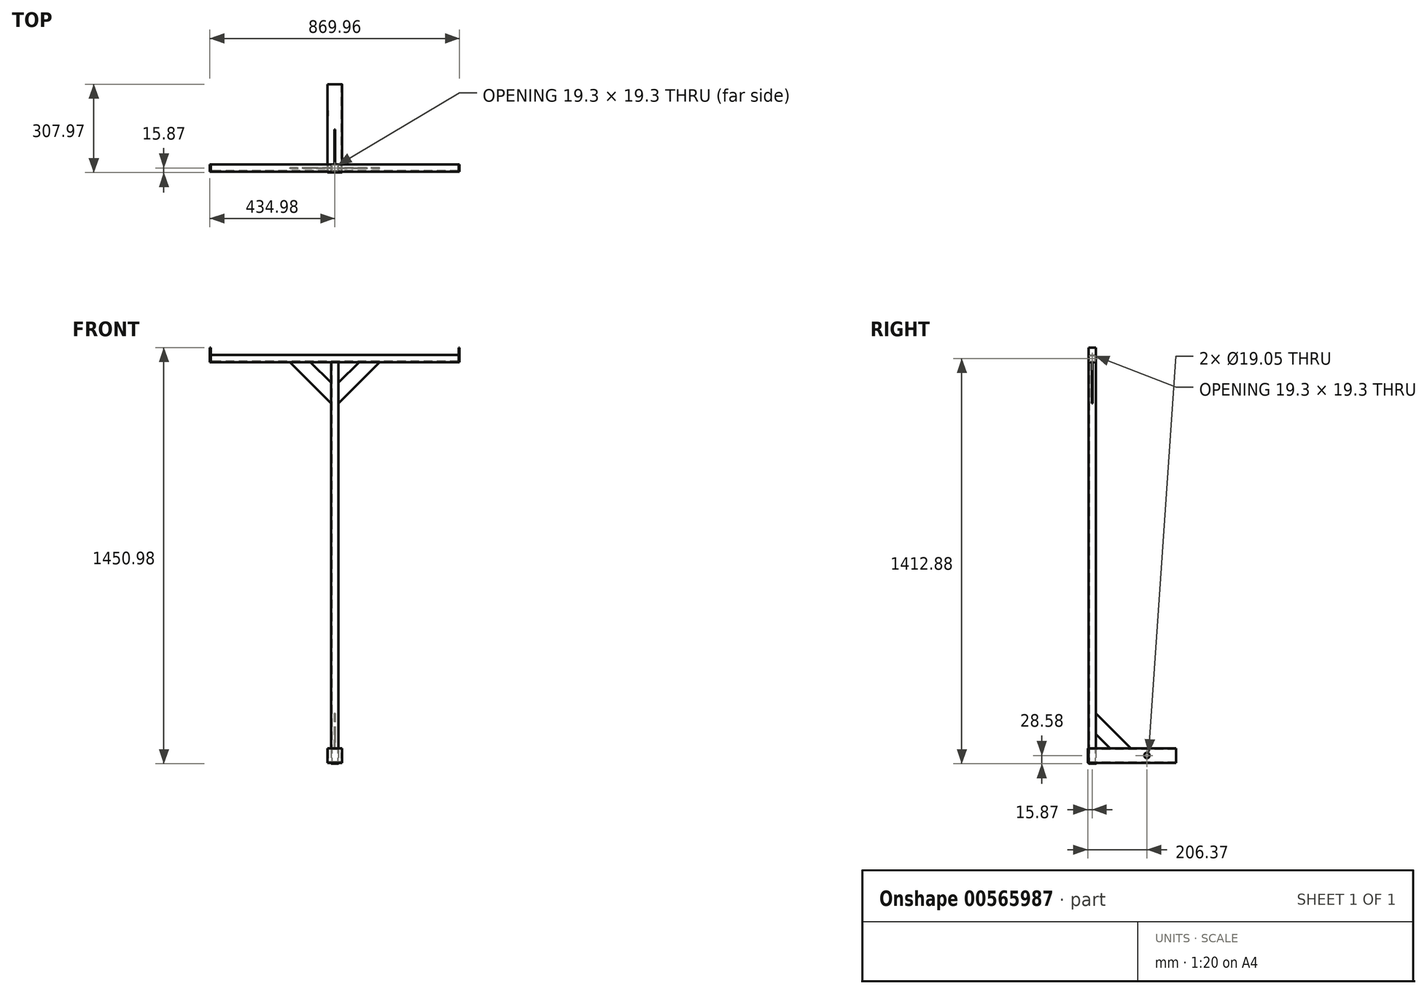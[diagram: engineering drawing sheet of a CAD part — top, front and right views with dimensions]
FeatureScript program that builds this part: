
annotation { "Feature Type Name" : "Feature", "Feature Type Description" : "" }
export const myFeature = defineFeature(function(context is Context, id is Id, definition is map)
    precondition{}
    {
        {
            var Q0;
            Q0=qCreatedBy(makeId("Front.planeOp"),FACE);
            var sketch = newSketch(context, id + "F0", { "sketchPlane" : qUnion([Q0])});
            skLineSegment(sketch, "E0.bottom", {"start": v(20.32, 25.4) * mm, "end": v(-20.32, 25.4) * mm});
            skLineSegment(sketch, "E0.top", {"start": v(20.32, -25.4) * mm, "end": v(-20.32, -25.4) * mm});
            skLineSegment(sketch, "E0.left", {"start": v(25.4, 20.32) * mm, "end": v(25.4, -20.32) * mm});
            skLineSegment(sketch, "E0.right", {"start": v(-25.4, 20.32) * mm, "end": v(-25.4, -20.32) * mm});
            skPoint(sketch, "E1.visualSharp", {"position": v(-25.4, 25.4) * mm});
            skArc(sketch, "E1.filletArc", {"start": v(-20.32, 25.4) * mm, "mid": v(-23.91, 23.91) * mm, "end": v(-25.4, 20.32) * mm});
            skPoint(sketch, "E2.visualSharp", {"position": v(25.4, 25.4) * mm});
            skArc(sketch, "E2.filletArc", {"start": v(25.4, 20.32) * mm, "mid": v(23.91, 23.91) * mm, "end": v(20.32, 25.4) * mm});
            skPoint(sketch, "E3.visualSharp", {"position": v(25.4, -25.4) * mm});
            skArc(sketch, "E3.filletArc", {"start": v(20.32, -25.4) * mm, "mid": v(23.91, -23.91) * mm, "end": v(25.4, -20.32) * mm});
            skPoint(sketch, "E4.visualSharp", {"position": v(-25.4, -25.4) * mm});
            skArc(sketch, "E4.filletArc", {"start": v(-25.4, -20.32) * mm, "mid": v(-23.91, -23.91) * mm, "end": v(-20.32, -25.4) * mm});
            skLineSegment(sketch, "E5.0", {"start": v(20.32, -22.35) * mm, "end": v(-20.32, -22.35) * mm});
            skArc(sketch, "E5.1", {"start": v(-22.35, -20.32) * mm, "mid": v(-21.76, -21.76) * mm, "end": v(-20.32, -22.35) * mm});
            skArc(sketch, "E5.2", {"start": v(20.32, -22.35) * mm, "mid": v(21.76, -21.76) * mm, "end": v(22.35, -20.32) * mm});
            skLineSegment(sketch, "E5.3", {"start": v(-22.35, 20.32) * mm, "end": v(-22.35, -20.32) * mm});
            skLineSegment(sketch, "E5.4", {"start": v(22.35, 20.32) * mm, "end": v(22.35, -20.32) * mm});
            skArc(sketch, "E5.5", {"start": v(22.35, 20.32) * mm, "mid": v(21.76, 21.76) * mm, "end": v(20.32, 22.35) * mm});
            skLineSegment(sketch, "E5.6", {"start": v(20.32, 22.35) * mm, "end": v(-20.32, 22.35) * mm});
            skArc(sketch, "E5.7", {"start": v(-20.32, 22.35) * mm, "mid": v(-21.76, 21.76) * mm, "end": v(-22.35, 20.32) * mm});
            skSolve(sketch);
        }
        {
            var Q0;
            Q0 = qSketchRegion(id + "F0", true);
            extrude(context, id + "F1", {"entities" : qUnion([Q0]), "endBound" : BoundingType.SYMMETRIC, "depth" : 304.8 * mm, "offsetDistance" : 25.4 * mm});
        }
        {
            var Q0;
            Q0=qCreatedBy(makeId("Top.planeOp"),FACE);
            var sketch = newSketch(context, id + "F2", { "sketchPlane" : qUnion([Q0])});
            skLineSegment(sketch, "E6.bottom", {"start": v(12.7, -127) * mm, "end": v(-12.7, -127) * mm});
            skLineSegment(sketch, "E6.top", {"start": v(12.7, -152.4) * mm, "end": v(-12.7, -152.4) * mm});
            skLineSegment(sketch, "E6.left", {"start": v(12.7, -127) * mm, "end": v(12.7, -152.4) * mm});
            skLineSegment(sketch, "E6.right", {"start": v(-12.7, -127) * mm, "end": v(-12.7, -152.4) * mm});
            skPoint(sketch, "E6.middle", {"position": v(0, -139.7) * mm});
            skSolve(sketch);
        }
        {
            var Q0;
            Q0 = qSketchRegion(id + "F2", true);
            extrude(context, id + "F3", {"entities" : qUnion([Q0]), "operationType" : NewBodyOperationType.REMOVE, "endBound" : BoundingType.SYMMETRIC, "oppositeDirection" : true, "depth" : 50.8 * mm, "offsetDistance" : 25.4 * mm});
        }
        {
            var Q0;
            Q0=qCreatedBy(makeId("Right.planeOp"),FACE);
            var sketch = newSketch(context, id + "F4", { "sketchPlane" : qUnion([Q0])});
            skCircle(sketch, "E7", {"center": v(50.8, 0) * mm, "radius": 9.53 * mm});
            skSolve(sketch);
        }
        {
            var Q0;
            Q0=qCreatedBy(makeId("Top.planeOp"),FACE);
            var sketch = newSketch(context, id + "F5", { "sketchPlane" : qUnion([Q0])});
            skLineSegment(sketch, "E8.bottom", {"start": v(9.53, -127) * mm, "end": v(-9.52, -127) * mm});
            skLineSegment(sketch, "E8.top", {"start": v(9.53, -152.4) * mm, "end": v(-9.52, -152.4) * mm});
            skLineSegment(sketch, "E8.left", {"start": v(12.7, -130.18) * mm, "end": v(12.7, -149.22) * mm});
            skLineSegment(sketch, "E8.right", {"start": v(-12.7, -130.18) * mm, "end": v(-12.7, -149.22) * mm});
            skPoint(sketch, "E8.middle", {"position": v(0, -139.7) * mm});
            skPoint(sketch, "E9.visualSharp", {"position": v(-12.7, -127) * mm});
            skArc(sketch, "E9.filletArc", {"start": v(-9.52, -127) * mm, "mid": v(-11.77, -127.93) * mm, "end": v(-12.7, -130.18) * mm});
            skPoint(sketch, "E10.visualSharp", {"position": v(12.7, -127) * mm});
            skArc(sketch, "E10.filletArc", {"start": v(12.7, -130.18) * mm, "mid": v(11.77, -127.93) * mm, "end": v(9.53, -127) * mm});
            skPoint(sketch, "E11.visualSharp", {"position": v(12.7, -152.4) * mm});
            skArc(sketch, "E11.filletArc", {"start": v(9.53, -152.4) * mm, "mid": v(11.77, -151.47) * mm, "end": v(12.7, -149.22) * mm});
            skPoint(sketch, "E12.visualSharp", {"position": v(-12.7, -152.4) * mm});
            skArc(sketch, "E12.filletArc", {"start": v(-12.7, -149.22) * mm, "mid": v(-11.77, -151.47) * mm, "end": v(-9.52, -152.4) * mm});
            skArc(sketch, "E13.0", {"start": v(9.53, -149.35) * mm, "mid": v(9.61, -149.31) * mm, "end": v(9.65, -149.22) * mm});
            skLineSegment(sketch, "E13.1", {"start": v(9.65, -130.18) * mm, "end": v(9.65, -149.22) * mm});
            skLineSegment(sketch, "E13.2", {"start": v(9.53, -149.35) * mm, "end": v(-9.52, -149.35) * mm});
            skArc(sketch, "E13.3", {"start": v(9.65, -130.18) * mm, "mid": v(9.61, -130.09) * mm, "end": v(9.53, -130.05) * mm});
            skArc(sketch, "E13.4", {"start": v(-9.65, -149.22) * mm, "mid": v(-9.61, -149.31) * mm, "end": v(-9.52, -149.35) * mm});
            skLineSegment(sketch, "E13.5", {"start": v(-9.65, -130.18) * mm, "end": v(-9.65, -149.22) * mm});
            skArc(sketch, "E13.6", {"start": v(-9.52, -130.05) * mm, "mid": v(-9.61, -130.09) * mm, "end": v(-9.65, -130.18) * mm});
            skLineSegment(sketch, "E13.7", {"start": v(9.53, -130.05) * mm, "end": v(-9.52, -130.05) * mm});
            skSolve(sketch);
        }
        {
            var Q0;
            Q0 = qSketchRegion(id + "F5", true);
            extrude(context, id + "F6", {"entities" : qUnion([Q0]), "depth" : 1371.6 * mm, "offsetDistance" : 25.4 * mm});
        }
        {
            var Q0;
            Q0 = qSketchRegion(id + "F5", true);
            extrude(context, id + "F7", {"entities" : qUnion([Q0]), "operationType" : NewBodyOperationType.ADD, "oppositeDirection" : true, "depth" : 28.57 * mm, "offsetDistance" : 25.4 * mm});
        }
        {
            var Q0;
            Q0 = qSketchRegion(id + "F4", true);
            extrude(context, id + "F8", {"entities" : qUnion([Q0]), "operationType" : NewBodyOperationType.REMOVE, "endBound" : BoundingType.SYMMETRIC, "oppositeDirection" : true, "depth" : 50.8 * mm, "offsetDistance" : 25.4 * mm});
        }
        {
            var Q0;
            {var subQ0=sQuery(id+"F0.wireOp",EDGE,"E5.3");var subQ1=sQuery(id+"F0.wireOp",EDGE,"E5.0");var subQ2=sQuery(id+"F0.wireOp",EDGE,"E4.filletArc");var subQ3=sQuery(id+"F0.wireOp",EDGE,"E5.1");var subQ4=sQuery(id+"F0.wireOp",EDGE,"E0.bottom");var subQ5=sQuery(id+"F0.wireOp",EDGE,"E5.6");var subQ6=sQuery(id+"F0.wireOp",EDGE,"E0.right");var subQ7=sQuery(id+"F0.wireOp",EDGE,"E0.top");var subQ8=sQuery(id+"F0.wireOp",EDGE,"E5.7");var subQ9=sQuery(id+"F0.wireOp",EDGE,"E1.filletArc");Q0=makeQuery(id+"F3.boolean.opBoolean","SPLIT",FACE,{"disambiguationData":[TD([makeQuery(id+"F1.opExtrude","SWEPT_FACE",FACE,{"disambiguationData":[OSD([subQ6])]})])],"derivedFrom":makeQuery(id+"F1.opExtrude","CAP_FACE",FACE,{"disambiguationData":[OSD([subQ4,subQ7,sQuery(id+"F0.wireOp",EDGE,"E0.left"),subQ6,subQ9,sQuery(id+"F0.wireOp",EDGE,"E2.filletArc"),sQuery(id+"F0.wireOp",EDGE,"E3.filletArc"),subQ2,subQ1,subQ3,sQuery(id+"F0.wireOp",EDGE,"E5.2"),subQ0,sQuery(id+"F0.wireOp",EDGE,"E5.4"),sQuery(id+"F0.wireOp",EDGE,"E5.5"),subQ5,subQ8])],"isStart":false})});}
            var sketch = newSketch(context, id + "F9", { "sketchPlane" : qUnion([Q0])});
            skLineSegment(sketch, "E14.bottom", {"start": v(-25.4, 25.4) * mm, "end": v(25.4, 25.4) * mm});
            skLineSegment(sketch, "E14.top", {"start": v(-25.4, -25.4) * mm, "end": v(25.4, -25.4) * mm});
            skLineSegment(sketch, "E14.left", {"start": v(-25.4, 25.4) * mm, "end": v(-25.4, -25.4) * mm});
            skLineSegment(sketch, "E14.right", {"start": v(25.4, 25.4) * mm, "end": v(25.4, -25.4) * mm});
            skPoint(sketch, "E14.middle", {"position": v(0, 0) * mm});
            skSolve(sketch);
        }
        {
            var Q0;
            Q0 = qSketchRegion(id + "F9", true);
            extrude(context, id + "F10", {"entities" : qUnion([Q0]), "depth" : 3.17 * mm, "offsetDistance" : 25.4 * mm});
        }
        {
            var Q0;
            Q0=qCreatedBy(makeId("Right.planeOp"),FACE);
            var sketch = newSketch(context, id + "F11", { "sketchPlane" : qUnion([Q0])});
            skLineSegment(sketch, "E15", {"start": v(-5.77, 25.4) * mm, "end": v(-127, 146.63) * mm});
            skLineSegment(sketch, "E16", {"start": v(-127, 146.63) * mm, "end": v(-127, 74.8) * mm});
            skLineSegment(sketch, "E17", {"start": v(-127, 74.8) * mm, "end": v(-77.6, 25.4) * mm});
            skLineSegment(sketch, "E18", {"start": v(-77.6, 25.4) * mm, "end": v(-5.77, 25.4) * mm});
            skSolve(sketch);
        }
        {
            var Q0;
            Q0 = qSketchRegion(id + "F11", true);
            extrude(context, id + "F12", {"entities" : qUnion([Q0]), "endBound" : BoundingType.SYMMETRIC, "depth" : 3.17 * mm, "offsetDistance" : 25.4 * mm});
        }
        {
            var Q0;
            Q0=qCreatedBy(makeId("Right.planeOp"),FACE);
            var sketch = newSketch(context, id + "F13", { "sketchPlane" : qUnion([Q0])});
            skLineSegment(sketch, "E19.bottom", {"start": v(-149.22, 1371.6) * mm, "end": v(-130.17, 1371.6) * mm});
            skLineSegment(sketch, "E19.top", {"start": v(-149.23, 1397) * mm, "end": v(-130.18, 1397) * mm});
            skLineSegment(sketch, "E19.left", {"start": v(-152.4, 1374.78) * mm, "end": v(-152.4, 1393.83) * mm});
            skLineSegment(sketch, "E19.right", {"start": v(-127, 1374.78) * mm, "end": v(-127, 1393.83) * mm});
            skPoint(sketch, "E19.middle", {"position": v(-139.7, 1384.3) * mm});
            skPoint(sketch, "E20.visualSharp", {"position": v(-127, 1397) * mm});
            skArc(sketch, "E20.filletArc", {"start": v(-127, 1393.83) * mm, "mid": v(-127.93, 1396.07) * mm, "end": v(-130.18, 1397) * mm});
            skPoint(sketch, "E21.visualSharp", {"position": v(-152.4, 1397) * mm});
            skArc(sketch, "E21.filletArc", {"start": v(-149.23, 1397) * mm, "mid": v(-151.47, 1396.07) * mm, "end": v(-152.4, 1393.83) * mm});
            skPoint(sketch, "E22.visualSharp", {"position": v(-152.4, 1371.6) * mm});
            skArc(sketch, "E22.filletArc", {"start": v(-152.4, 1374.78) * mm, "mid": v(-151.47, 1372.53) * mm, "end": v(-149.22, 1371.6) * mm});
            skPoint(sketch, "E23.visualSharp", {"position": v(-127, 1371.6) * mm});
            skArc(sketch, "E23.filletArc", {"start": v(-130.17, 1371.6) * mm, "mid": v(-127.93, 1372.53) * mm, "end": v(-127, 1374.78) * mm});
            skArc(sketch, "E24.0", {"start": v(-149.35, 1374.78) * mm, "mid": v(-149.31, 1374.69) * mm, "end": v(-149.22, 1374.65) * mm});
            skLineSegment(sketch, "E24.1", {"start": v(-149.35, 1374.78) * mm, "end": v(-149.35, 1393.83) * mm});
            skLineSegment(sketch, "E24.2", {"start": v(-149.22, 1374.65) * mm, "end": v(-130.17, 1374.65) * mm});
            skArc(sketch, "E24.3", {"start": v(-149.23, 1393.95) * mm, "mid": v(-149.31, 1393.91) * mm, "end": v(-149.35, 1393.83) * mm});
            skArc(sketch, "E24.4", {"start": v(-130.17, 1374.65) * mm, "mid": v(-130.09, 1374.69) * mm, "end": v(-130.05, 1374.78) * mm});
            skLineSegment(sketch, "E24.5", {"start": v(-130.05, 1374.78) * mm, "end": v(-130.05, 1393.83) * mm});
            skArc(sketch, "E24.6", {"start": v(-130.05, 1393.83) * mm, "mid": v(-130.09, 1393.91) * mm, "end": v(-130.18, 1393.95) * mm});
            skLineSegment(sketch, "E24.7", {"start": v(-149.23, 1393.95) * mm, "end": v(-130.18, 1393.95) * mm});
            skSolve(sketch);
        }
        {
            var Q0;
            Q0 = qSketchRegion(id + "F13", true);
            extrude(context, id + "F14", {"entities" : qUnion([Q0]), "endBound" : BoundingType.SYMMETRIC, "depth" : 863.6 * mm, "offsetDistance" : 25.4 * mm});
        }
        {
            var Q0;
            Q0=qCreatedBy(makeId("Front.planeOp"),FACE);
            cPlane(context, id + "F15", {"entities" : qUnion([Q0]), "cplaneType" : CPlaneType.OFFSET, "offset" : 139.7 * mm, "width" : 152.4 * mm, "height" : 152.4 * mm});
        }
        {
            var Q0;
            Q0=qCreatedBy(id+"F15.planeOp",FACE);
            var sketch = newSketch(context, id + "F16", { "sketchPlane" : qUnion([Q0])});
            skLineSegment(sketch, "E25", {"start": v(-156.38, 1371.6) * mm, "end": v(-12.7, 1227.92) * mm});
            skLineSegment(sketch, "E26", {"start": v(-12.7, 1227.92) * mm, "end": v(-12.7, 1299.76) * mm});
            skLineSegment(sketch, "E27", {"start": v(-12.7, 1299.76) * mm, "end": v(-84.54, 1371.6) * mm});
            skLineSegment(sketch, "E28", {"start": v(-84.54, 1371.6) * mm, "end": v(-156.38, 1371.6) * mm});
            skSolve(sketch);
        }
        {
            var Q0;
            Q0 = qSketchRegion(id + "F16", true);
            extrude(context, id + "F17", {"entities" : qUnion([Q0]), "endBound" : BoundingType.SYMMETRIC, "depth" : 3.17 * mm, "offsetDistance" : 25.4 * mm});
        }
        {
            var Q0;
            Q0=makeQuery(id+"F17.opExtrude","SWEPT_BODY",BODY,{"disambiguationData":[OSD([sQuery(id+"F16.wireOp",EDGE,"E25"),sQuery(id+"F16.wireOp",EDGE,"E26"),sQuery(id+"F16.wireOp",EDGE,"E27"),sQuery(id+"F16.wireOp",EDGE,"E28")])]});
            var Q1;
            Q1=qCreatedBy(makeId("Right.planeOp"),FACE);
            mirror(context, id + "F18", {"entities" : qUnion([Q0]), "mirrorPlane" : qUnion([Q1])});
        }
        {
            var Q0;
            Q0=makeQuery(id+"F14.opExtrude","CAP_FACE",FACE,{"disambiguationData":[OSD([sQuery(id+"F13.wireOp",EDGE,"E19.bottom"),sQuery(id+"F13.wireOp",EDGE,"E19.top"),sQuery(id+"F13.wireOp",EDGE,"E19.left"),sQuery(id+"F13.wireOp",EDGE,"E19.right"),sQuery(id+"F13.wireOp",EDGE,"E20.filletArc"),sQuery(id+"F13.wireOp",EDGE,"E21.filletArc"),sQuery(id+"F13.wireOp",EDGE,"E22.filletArc"),sQuery(id+"F13.wireOp",EDGE,"E23.filletArc"),sQuery(id+"F13.wireOp",EDGE,"E24.0"),sQuery(id+"F13.wireOp",EDGE,"E24.1"),sQuery(id+"F13.wireOp",EDGE,"E24.2"),sQuery(id+"F13.wireOp",EDGE,"E24.3"),sQuery(id+"F13.wireOp",EDGE,"E24.4"),sQuery(id+"F13.wireOp",EDGE,"E24.5"),sQuery(id+"F13.wireOp",EDGE,"E24.6"),sQuery(id+"F13.wireOp",EDGE,"E24.7")])],"isStart":true});
            var sketch = newSketch(context, id + "F19", { "sketchPlane" : qUnion([Q0])});
            skLineSegment(sketch, "E29.bottom", {"start": v(152.4, 1371.6) * mm, "end": v(127, 1371.6) * mm});
            skLineSegment(sketch, "E29.top", {"start": v(152.4, 1422.4) * mm, "end": v(127, 1422.4) * mm});
            skLineSegment(sketch, "E29.left", {"start": v(152.4, 1371.6) * mm, "end": v(152.4, 1422.4) * mm});
            skLineSegment(sketch, "E29.right", {"start": v(127, 1371.6) * mm, "end": v(127, 1422.4) * mm});
            skPoint(sketch, "E29.middle", {"position": v(139.7, 1397) * mm});
            skSolve(sketch);
        }
        {
            var Q0;
            Q0 = qSketchRegion(id + "F19", true);
            extrude(context, id + "F20", {"entities" : qUnion([Q0]), "depth" : 3.17 * mm, "offsetDistance" : 25.4 * mm});
        }
        {
            var Q0;
            Q0=makeQuery(id+"F20.opExtrude","SWEPT_BODY",BODY,{"disambiguationData":[OSD([sQuery(id+"F19.wireOp",EDGE,"E29.bottom"),sQuery(id+"F19.wireOp",EDGE,"E29.top"),sQuery(id+"F19.wireOp",EDGE,"E29.left"),sQuery(id+"F19.wireOp",EDGE,"E29.right")])]});
            var Q1;
            Q1=qCreatedBy(makeId("Right.planeOp"),FACE);
            mirror(context, id + "F21", {"entities" : qUnion([Q0]), "mirrorPlane" : qUnion([Q1])});
        }
    });
